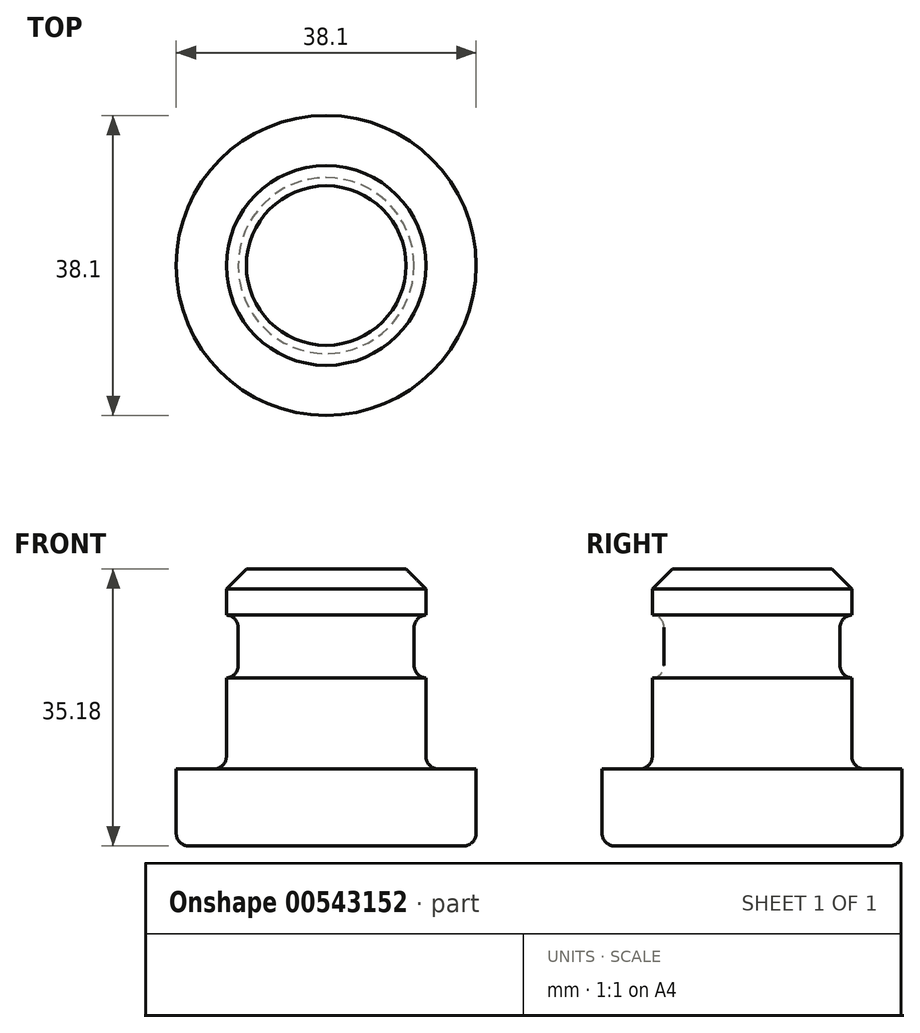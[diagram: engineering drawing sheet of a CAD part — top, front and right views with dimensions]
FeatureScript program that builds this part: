
annotation { "Feature Type Name" : "Feature", "Feature Type Description" : "" }
export const myFeature = defineFeature(function(context is Context, id is Id, definition is map)
    precondition{}
    {
        {
            var Q0;
            Q0=qCreatedBy(makeId("Front.planeOp"),FACE);
            var sketch = newSketch(context, id + "F0", { "sketchPlane" : qUnion([Q0])});
            skLineSegment(sketch, "E0", {"start": v(0, 29.67) * mm, "end": v(0, -25.5) * mm, "construction": true});
            skLineSegment(sketch, "E1", {"start": v(0, 20.48) * mm, "end": v(12.67, 20.48) * mm});
            skLineSegment(sketch, "E2", {"start": v(12.67, 20.48) * mm, "end": v(12.67, 14.64) * mm});
            skLineSegment(sketch, "E3", {"start": v(14.26, -4.92) * mm, "end": v(19.05, -4.92) * mm});
            skLineSegment(sketch, "E4", {"start": v(19.05, -4.92) * mm, "end": v(19.05, -14.7) * mm});
            skLineSegment(sketch, "E5", {"start": v(19.05, -14.7) * mm, "end": v(0, -14.7) * mm});
            skLineSegment(sketch, "E6", {"start": v(12.76, 14.64) * mm, "end": v(12.67, 14.64) * mm});
            skLineSegment(sketch, "E7", {"start": v(11.18, 13.05) * mm, "end": v(11.18, 8.22) * mm});
            skLineSegment(sketch, "E8", {"start": v(12.67, 6.64) * mm, "end": v(12.76, 6.64) * mm});
            skPoint(sketch, "E9.visualSharp", {"position": v(11.18, 14.64) * mm});
            skArc(sketch, "E9.filletArc", {"start": v(12.76, 14.64) * mm, "mid": v(11.64, 14.17) * mm, "end": v(11.18, 13.05) * mm});
            skPoint(sketch, "E10.visualSharp", {"position": v(11.18, 6.64) * mm});
            skArc(sketch, "E10.filletArc", {"start": v(11.18, 8.22) * mm, "mid": v(11.64, 7.1) * mm, "end": v(12.76, 6.64) * mm});
            skPoint(sketch, "E11.visualSharp", {"position": v(12.67, -4.92) * mm});
            skArc(sketch, "E11.filletArc", {"start": v(12.67, -3.33) * mm, "mid": v(13.14, -4.46) * mm, "end": v(14.26, -4.92) * mm});
            skLineSegment(sketch, "E12.trimOffspring", {"start": v(12.67, 6.64) * mm, "end": v(12.67, -3.33) * mm});
            skLineSegment(sketch, "E13", {"start": v(0, 20.48) * mm, "end": v(0, -14.7) * mm});
            skSolve(sketch);
        }
        {
            var Q0;
            {var subQ7=sQuery(id+"F0.wireOp",EDGE,"E1");Q0=makeQuery(id+"F0.imprint","IMPRINT",FACE,{"disambiguationData":[TD([[makeQuery(id+"F0.imprint","IMPRINT",EDGE,{"derivedFrom":subQ7}),-1.0]])]});}
            var Q1;
            Q1=sQuery(id+"F0.wireOp",EDGE,"E0");
            revolve(context, id + "F1", {"entities" : qUnion([Q0]), "axis" : qUnion([Q1]), "revolveType" : RevolveType.FULL});
        }
        {
            var Q0;
            Q0=makeQuery(id+"F1.opRevolve","SWEPT_EDGE",EDGE,{"disambiguationData":[OSD([sQuery(id+"F0.wireOp",EDGE,"E1"),sQuery(id+"F0.wireOp",EDGE,"E2")])]});
            chamfer(context, id + "F2", {"entities" : qUnion([Q0]), "width" : 2.54 * mm, "tangentPropagation" : true});
        }
        {
            var Q0;
            Q0=makeQuery(id+"F1.opRevolve","SWEPT_EDGE",EDGE,{"disambiguationData":[OSD([sQuery(id+"F0.wireOp",EDGE,"E4"),sQuery(id+"F0.wireOp",EDGE,"E5")])]});
            fillet(context, id + "F3", {"entities" : qUnion([Q0]), "radius" : 1.59 * mm, "tangentPropagation" : true, "allowEdgeOverflow" : false});
        }
    });
